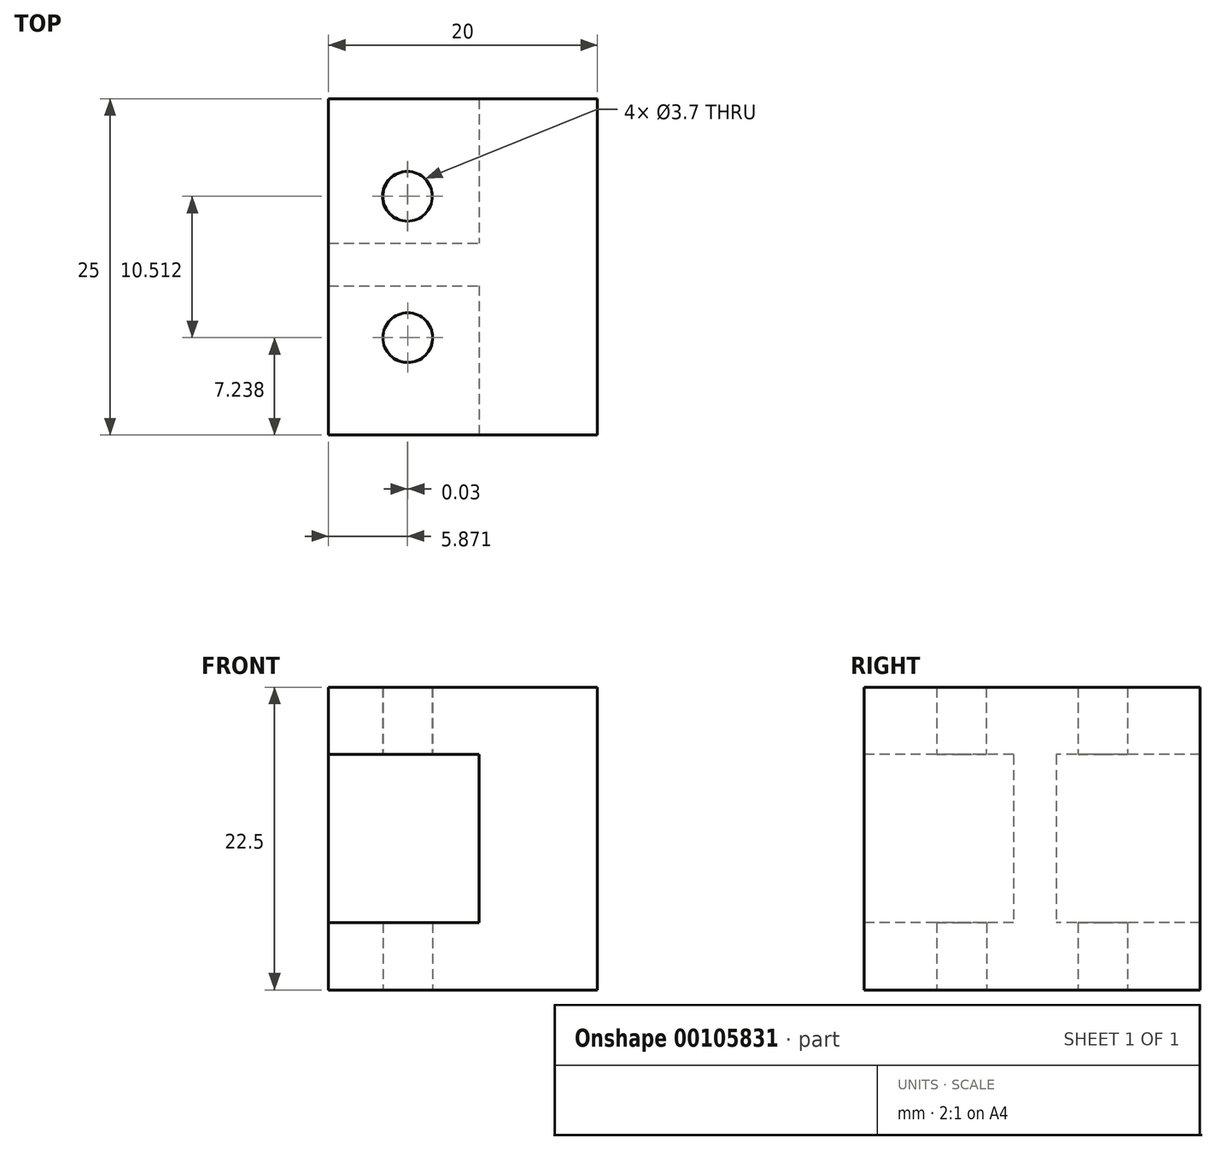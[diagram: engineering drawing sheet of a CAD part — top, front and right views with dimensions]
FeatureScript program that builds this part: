
annotation { "Feature Type Name" : "Feature", "Feature Type Description" : "" }
export const myFeature = defineFeature(function(context is Context, id is Id, definition is map)
    precondition{}
    {
        {
            var Q0;
            Q0=qCreatedBy(makeId("Top.planeOp"),FACE);
            var sketch = newSketch(context, id + "F0", { "sketchPlane" : qUnion([Q0])});
            skLineSegment(sketch, "E0.bottom", {"start": v(-27.2, 7.25) * mm, "end": v(-7.2, 7.25) * mm});
            skLineSegment(sketch, "E0.top", {"start": v(-27.2, -17.75) * mm, "end": v(-7.2, -17.75) * mm});
            skLineSegment(sketch, "E0.left", {"start": v(-27.2, 7.25) * mm, "end": v(-27.2, -17.75) * mm});
            skLineSegment(sketch, "E0.right", {"start": v(-7.2, 7.25) * mm, "end": v(-7.2, -17.75) * mm});
            skCircle(sketch, "E1", {"center": v(-21.3, 0) * mm, "radius": 1.85 * mm});
            skCircle(sketch, "E2", {"center": v(-21.3, -10.5) * mm, "radius": 1.85 * mm});
            skSolve(sketch);
        }
        {
            var Q0;
            Q0=qSketchRegion(id+"F0",true);
            extrude(context, id + "F1", {"entities" : qUnion([Q0]), "depth" : 5 * mm});
        }
        {
            var Q0;
            Q0=makeQuery(id+"F1.opExtrude","CAP_FACE",FACE,{"disambiguationData":[OSD([sQuery(id+"F0.wireOp",EDGE,"E0.bottom"),sQuery(id+"F0.wireOp",EDGE,"E0.top"),sQuery(id+"F0.wireOp",EDGE,"E0.left"),sQuery(id+"F0.wireOp",EDGE,"E0.right"),sQuery(id+"F0.wireOp",EDGE,"E1"),sQuery(id+"F0.wireOp",EDGE,"E2")])],"isStart":false});
            var sketch = newSketch(context, id + "F2", { "sketchPlane" : qUnion([Q0])});
            skLineSegment(sketch, "E3.bottom", {"start": v(-7.2, 7.25) * mm, "end": v(-15.99, 7.25) * mm});
            skLineSegment(sketch, "E3.top", {"start": v(-7.2, -17.75) * mm, "end": v(-15.99, -17.75) * mm});
            skLineSegment(sketch, "E3.left", {"start": v(-7.2, 7.25) * mm, "end": v(-7.2, -17.75) * mm});
            skLineSegment(sketch, "E3.right", {"start": v(-15.99, 7.25) * mm, "end": v(-15.99, -17.75) * mm});
            skLineSegment(sketch, "E4.bottom", {"start": v(-27.2, -3.47) * mm, "end": v(-15.99, -3.47) * mm});
            skLineSegment(sketch, "E4.top", {"start": v(-27.2, -6.65) * mm, "end": v(-15.99, -6.65) * mm});
            skLineSegment(sketch, "E4.left", {"start": v(-27.2, -3.47) * mm, "end": v(-27.2, -6.65) * mm});
            skLineSegment(sketch, "E4.right", {"start": v(-15.99, -3.47) * mm, "end": v(-15.99, -6.65) * mm});
            skSolve(sketch);
        }
        {
            var Q0;
            Q0=makeQuery(id+"F2.imprint","IMPRINT",FACE,{"disambiguationData":[TD([[makeQuery(id+"F2.imprint","IMPRINT",EDGE,{"derivedFrom":sQuery(id+"F2.wireOp",EDGE,"E4.bottom")}),-1.0]])]});
            var Q1;
            {var subQ1=sQuery(id+"F2.wireOp",EDGE,"E3.bottom");Q1=makeQuery(id+"F2.imprint","IMPRINT",FACE,{"disambiguationData":[TD([[makeQuery(id+"F2.imprint","IMPRINT",EDGE,{"derivedFrom":subQ1}),-1.0]])]});}
            var Q2;
            Q2=sQuery(id+"F2.wireOp",EDGE,"E4.left");
            var Q3;
            Q3=sQuery(id+"F2.wireOp",EDGE,"E4.top");
            var Q4;
            Q4=sQuery(id+"F2.wireOp",EDGE,"E4.bottom");
            var Q5;
            Q5=sQuery(id+"F2.wireOp",EDGE,"E3.right");
            extrude(context, id + "F3", {"entities" : qUnion([Q0, Q1]), "operationType" : NewBodyOperationType.ADD, "surfaceEntities" : qUnion([Q2, Q3, Q4, Q5]), "depth" : 12.5 * mm});
        }
        {
            var Q0;
            Q0=makeQuery(id+"F3.opExtrude","CAP_FACE",FACE,{"disambiguationData":[OSD([sQuery(id+"F2.wireOp",EDGE,"E3.bottom"),sQuery(id+"F2.wireOp",EDGE,"E3.top"),sQuery(id+"F2.wireOp",EDGE,"E3.left"),sQuery(id+"F2.wireOp",EDGE,"E3.right"),sQuery(id+"F2.wireOp",EDGE,"E4.bottom"),sQuery(id+"F2.wireOp",EDGE,"E4.top"),sQuery(id+"F2.wireOp",EDGE,"E4.left")])],"isStart":false});
            var sketch = newSketch(context, id + "F4", { "sketchPlane" : qUnion([Q0])});
            skLineSegment(sketch, "E5.bottom", {"start": v(-7.2, 7.25) * mm, "end": v(-27.2, 7.25) * mm});
            skLineSegment(sketch, "E5.top", {"start": v(-7.2, -17.75) * mm, "end": v(-27.2, -17.75) * mm});
            skLineSegment(sketch, "E5.left", {"start": v(-7.2, 7.25) * mm, "end": v(-7.2, -17.75) * mm});
            skLineSegment(sketch, "E5.right", {"start": v(-27.2, 7.25) * mm, "end": v(-27.2, -17.75) * mm});
            skCircle(sketch, "E6", {"center": v(-21.33, 0) * mm, "radius": 1.85 * mm});
            skCircle(sketch, "E7", {"center": v(-21.3, -10.51) * mm, "radius": 1.85 * mm});
            skSolve(sketch);
        }
        {
            var Q0;
            Q0=qSketchRegion(id+"F4",true);
            extrude(context, id + "F5", {"entities" : qUnion([Q0]), "operationType" : NewBodyOperationType.ADD, "depth" : 5 * mm});
        }
    });
